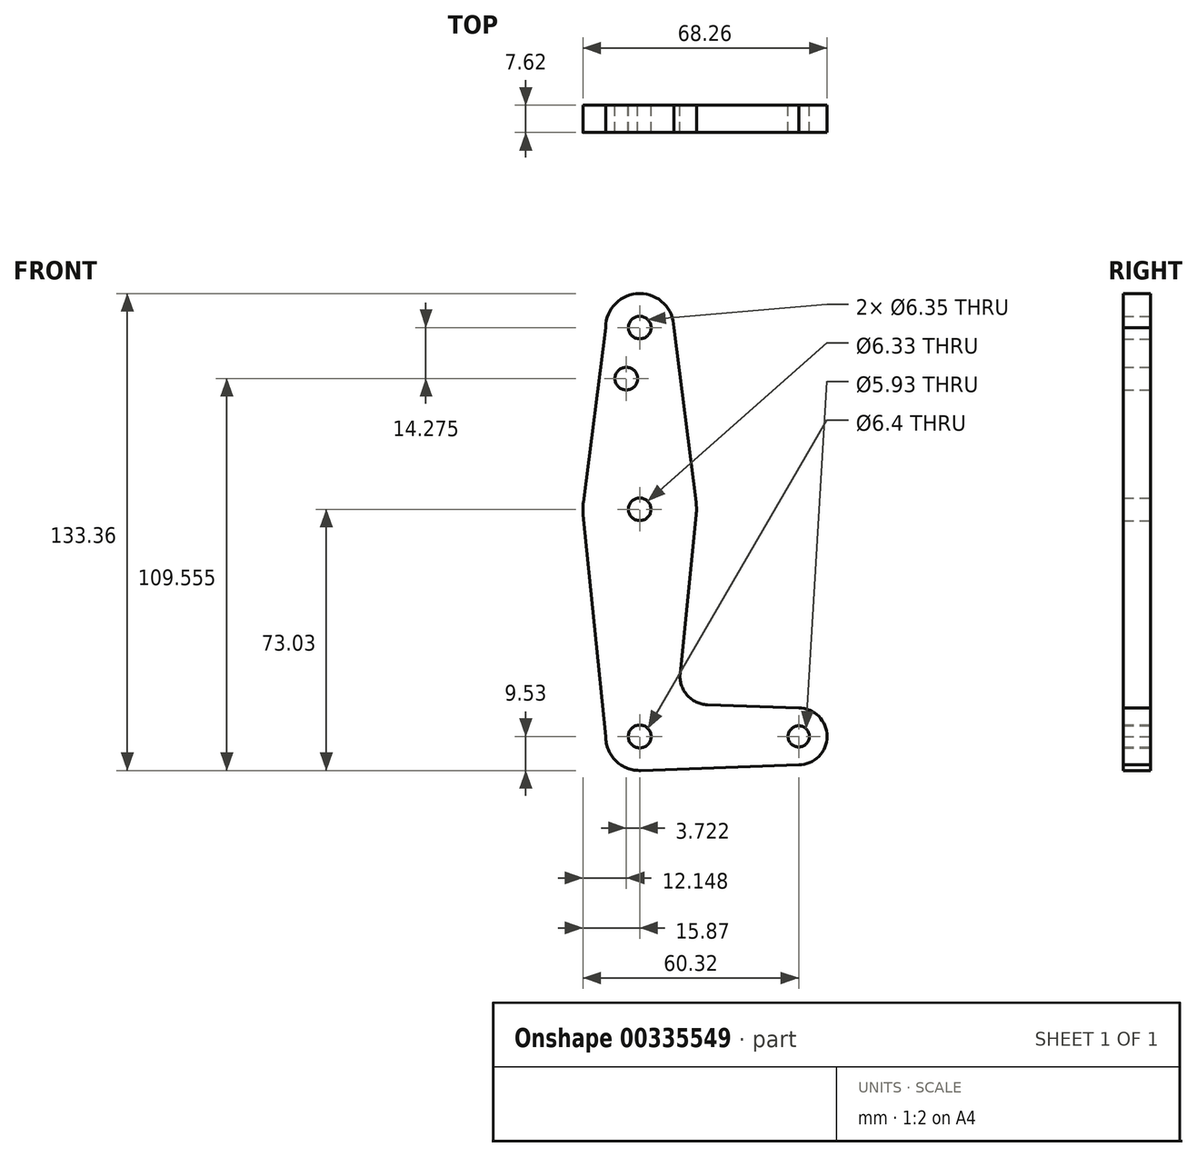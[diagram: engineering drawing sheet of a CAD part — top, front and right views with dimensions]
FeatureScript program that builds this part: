
annotation { "Feature Type Name" : "Feature", "Feature Type Description" : "" }
export const myFeature = defineFeature(function(context is Context, id is Id, definition is map)
    precondition{}
    {
        {
            var Q0;
            Q0=qCreatedBy(makeId("Front.planeOp"),FACE);
            var sketch = newSketch(context, id + "F0", { "sketchPlane" : qUnion([Q0])});
            skCircle(sketch, "E0", {"center": v(0, 0) * mm, "radius": 9.53 * mm});
            skCircle(sketch, "E1", {"center": v(44.45, 0) * mm, "radius": 7.94 * mm});
            skCircle(sketch, "E2", {"center": v(0, 63.5) * mm, "radius": 15.88 * mm});
            skCircle(sketch, "E3", {"center": v(0, 114.3) * mm, "radius": 9.53 * mm});
            skCircle(sketch, "E4", {"center": v(0, 114.3) * mm, "radius": 3.18 * mm});
            skCircle(sketch, "E5", {"center": v(0, 63.5) * mm, "radius": 3.17 * mm});
            skCircle(sketch, "E6", {"center": v(0, 0) * mm, "radius": 3.2 * mm});
            skCircle(sketch, "E7", {"center": v(44.45, 0) * mm, "radius": 2.97 * mm});
            skLineSegment(sketch, "E8", {"start": v(0, 114.3) * mm, "end": v(0, 0) * mm, "construction": true});
            skLineSegment(sketch, "E9", {"start": v(0, 0) * mm, "end": v(44.45, 0) * mm, "construction": true});
            skCircle(sketch, "E10", {"center": v(-3.72, 100.03) * mm, "radius": 3.18 * mm});
            skLineSegment(sketch, "E11", {"start": v(-9.53, 114.3) * mm, "end": v(-15.75, 65.5) * mm});
            skLineSegment(sketch, "E12", {"start": v(9.52, 114.3) * mm, "end": v(15.75, 65.5) * mm});
            skLineSegment(sketch, "E13", {"start": v(44.45, 7.94) * mm, "end": v(18.93, 8.85) * mm});
            skLineSegment(sketch, "E14", {"start": v(44.45, -7.94) * mm, "end": v(0, -9.53) * mm});
            skLineSegment(sketch, "E15", {"start": v(-9.53, 0) * mm, "end": v(-15.8, 61.9) * mm});
            skLineSegment(sketch, "E16", {"start": v(11.3, 17.6) * mm, "end": v(15.8, 61.9) * mm});
            skArc(sketch, "E17.filletArc", {"start": v(11.3, 17.6) * mm, "mid": v(13.22, 11.57) * mm, "end": v(18.93, 8.85) * mm});
            skSolve(sketch);
        }
        {
            var Q0;
            Q0 = qSketchRegion(id + "F0", true);
            extrude(context, id + "F1", {"entities" : qUnion([Q0]), "flatOperationType" : FlatOperationType.REMOVE, "offsetDistance" : 25.4 * mm, "depth" : 7.62 * mm, "domain" : OperationDomain.MODEL});
        }
    });
